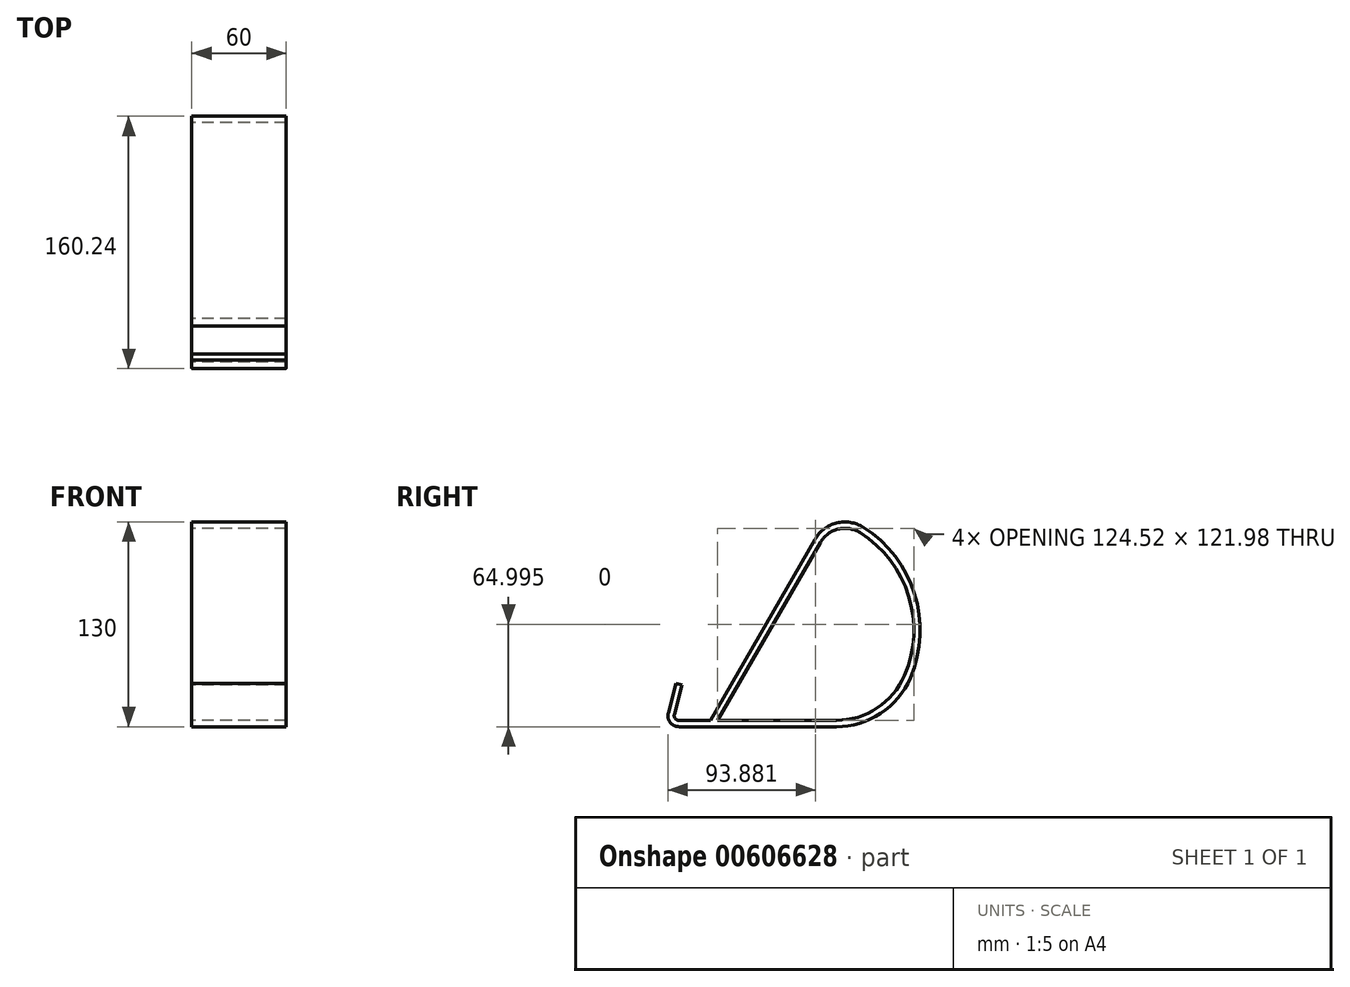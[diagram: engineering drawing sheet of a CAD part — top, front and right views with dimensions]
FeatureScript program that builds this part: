
annotation { "Feature Type Name" : "Feature", "Feature Type Description" : "" }
export const myFeature = defineFeature(function(context is Context, id is Id, definition is map)
    precondition{}
    {
        {
            var Q0;
            Q0=qCreatedBy(makeId("Right.planeOp"),FACE);
            var sketch = newSketch(context, id + "F0", { "sketchPlane" : qUnion([Q0])});
            skLineSegment(sketch, "E0", {"start": v(-55.08, -59.4) * mm, "end": v(11.89, 56.6) * mm, "construction": true});
            skLineSegment(sketch, "E1", {"start": v(-55.08, -59.4) * mm, "end": v(-76.24, -59.4) * mm, "construction": true});
            skArc(sketch, "E2", {"start": v(-81.07, -53.1) * mm, "mid": v(-80.2, -57.44) * mm, "end": v(-76.24, -59.4) * mm, "construction": true});
            skLineSegment(sketch, "E3", {"start": v(-81.07, -53.1) * mm, "end": v(-76.06, -34.4) * mm, "construction": true});
            skLineSegment(sketch, "E4", {"start": v(-55.08, -59.4) * mm, "end": v(23.7, -59.4) * mm, "construction": true});
            skArc(sketch, "E5.filletArc", {"start": v(39.83, 63.55) * mm, "mid": v(24.38, 66.01) * mm, "end": v(11.89, 56.6) * mm, "construction": true});
            skPoint(sketch, "E6.visualSharp", {"position": v(40.96, 97.02) * mm});
            skArc(sketch, "E7.filletArc", {"start": v(23.7, -59.4) * mm, "mid": v(50.76, -51.28) * mm, "end": v(68.9, -29.62) * mm, "construction": true});
            skArc(sketch, "E8", {"start": v(68.9, -29.62) * mm, "mid": v(71.6, 22.34) * mm, "end": v(39.83, 63.55) * mm, "construction": true});
            skLineSegment(sketch, "E9.0", {"start": v(-79.14, -53.62) * mm, "end": v(-74.12, -34.91) * mm});
            skLineSegment(sketch, "E9.1", {"start": v(-56.24, -57.4) * mm, "end": v(-76.24, -57.4) * mm});
            skArc(sketch, "E9.2", {"start": v(23.7, -61.4) * mm, "mid": v(51.86, -52.95) * mm, "end": v(70.74, -30.4) * mm});
            skArc(sketch, "E9.3", {"start": v(70.74, -30.4) * mm, "mid": v(73.5, 22.94) * mm, "end": v(40.9, 65.24) * mm});
            skArc(sketch, "E9.4", {"start": v(40.9, 65.24) * mm, "mid": v(23.9, 67.95) * mm, "end": v(10.16, 57.6) * mm});
            skLineSegment(sketch, "E9.5", {"start": v(-56.24, -57.4) * mm, "end": v(10.16, 57.6) * mm});
            skLineSegment(sketch, "E10.1", {"start": v(23.7, -61.4) * mm, "end": v(-76.24, -61.4) * mm});
            skLineSegment(sketch, "E11.0", {"start": v(-83, -52.59) * mm, "end": v(-77.99, -33.88) * mm});
            skArc(sketch, "E11.1", {"start": v(-83, -52.59) * mm, "mid": v(-81.8, -58.66) * mm, "end": v(-76.24, -61.4) * mm});
            skArc(sketch, "E12.0", {"start": v(38.77, 61.85) * mm, "mid": v(24.87, 64.07) * mm, "end": v(13.62, 55.6) * mm});
            skLineSegment(sketch, "E12.1", {"start": v(-51.62, -57.4) * mm, "end": v(13.62, 55.6) * mm});
            skArc(sketch, "E12.2", {"start": v(67.07, -28.83) * mm, "mid": v(69.69, 21.75) * mm, "end": v(38.77, 61.85) * mm});
            skArc(sketch, "E12.3", {"start": v(23.7, -57.4) * mm, "mid": v(49.66, -49.61) * mm, "end": v(67.07, -28.83) * mm});
            skLineSegment(sketch, "E12.4", {"start": v(-51.62, -57.4) * mm, "end": v(23.7, -57.4) * mm});
            skLineSegment(sketch, "E13", {"start": v(-77.99, -33.88) * mm, "end": v(-74.12, -34.91) * mm});
            skArc(sketch, "E14.0", {"start": v(-79.14, -53.62) * mm, "mid": v(-78.62, -56.22) * mm, "end": v(-76.24, -57.4) * mm});
            skLineSegment(sketch, "E15", {"start": v(77, 68.6) * mm, "end": v(-25.17, 68.6) * mm, "construction": true});
            skLineSegment(sketch, "E16", {"start": v(77, 68.6) * mm, "end": v(77, -33.83) * mm, "construction": true});
            skSolve(sketch);
        }
        {
            var Q0;
            Q0=qSketchRegion(id+"F0",true);
            extrude(context, id + "F1", {"entities" : qUnion([Q0]), "endBound" : BoundingType.SYMMETRIC, "depth" : 60 * mm, "offsetDistance" : 25 * mm});
        }
    });
